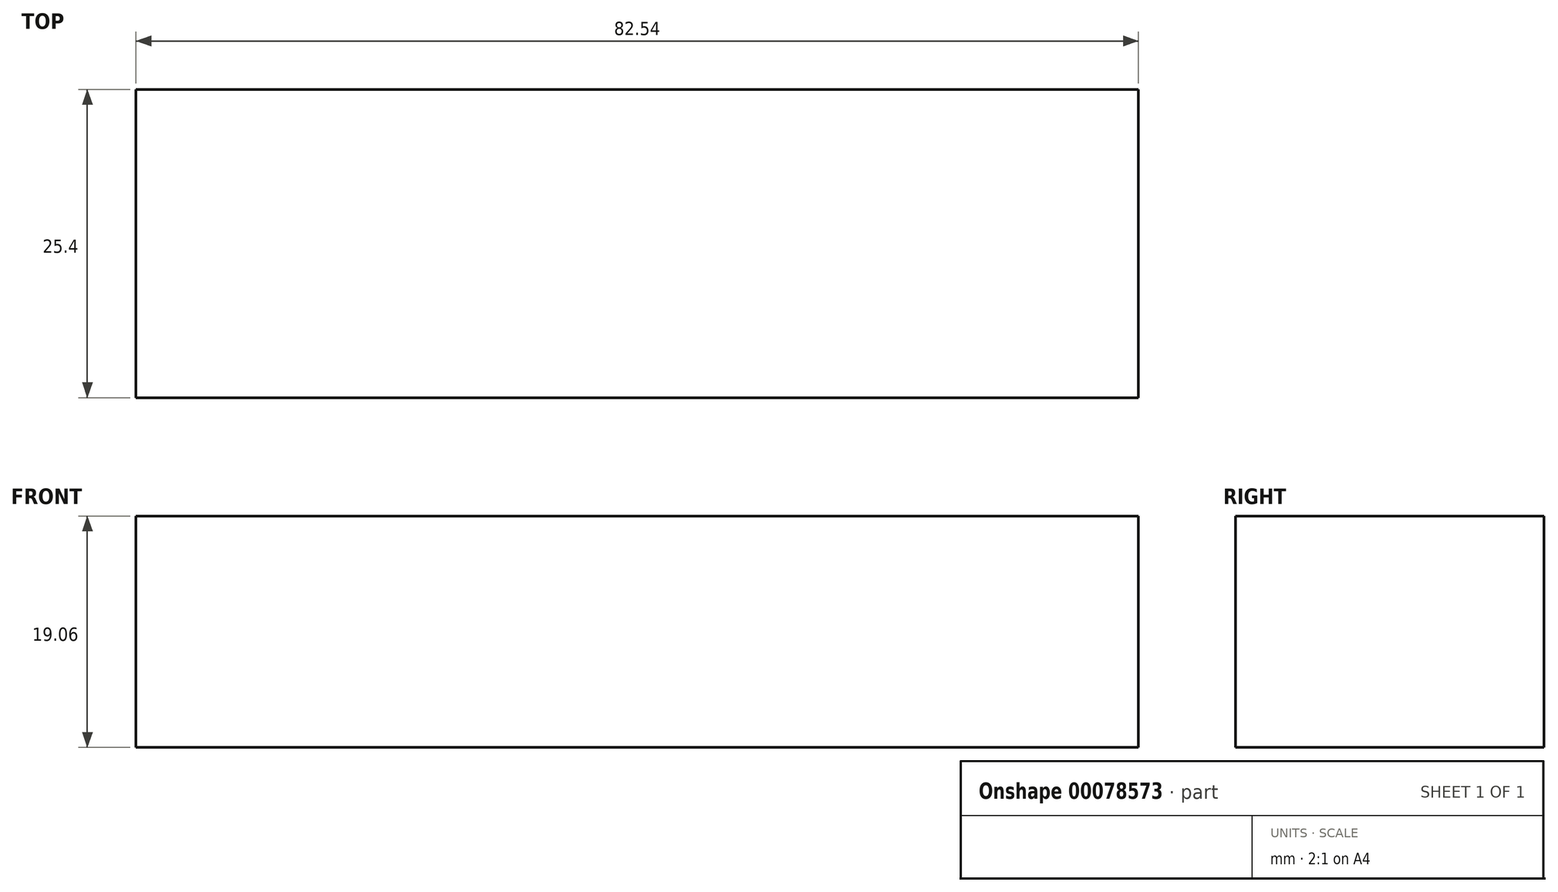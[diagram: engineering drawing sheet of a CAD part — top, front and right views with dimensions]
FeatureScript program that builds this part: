
annotation { "Feature Type Name" : "Feature", "Feature Type Description" : "" }
export const myFeature = defineFeature(function(context is Context, id is Id, definition is map)
    precondition{}
    {
        {
            var Q0;
            Q0=qCreatedBy(makeId("Front.planeOp"),FACE);
            var sketch = newSketch(context, id + "F0", { "sketchPlane" : qUnion([Q0])});
            skLineSegment(sketch, "E0.bottom", {"start": v(41.28, 9.53) * mm, "end": v(-41.28, 9.53) * mm});
            skLineSegment(sketch, "E0.top", {"start": v(41.28, -9.52) * mm, "end": v(-41.27, -9.52) * mm});
            skLineSegment(sketch, "E0.left", {"start": v(41.28, 9.53) * mm, "end": v(41.28, -9.52) * mm});
            skLineSegment(sketch, "E0.right", {"start": v(-41.28, 9.53) * mm, "end": v(-41.27, -9.52) * mm});
            skPoint(sketch, "E0.middle", {"position": v(0, 0) * mm});
            skSolve(sketch);
        }
        {
            var Q0;
            Q0=makeQuery(id+"F0.imprint","IMPRINT",FACE,{"disambiguationData":[TD([[makeQuery(id+"F0.imprint","IMPRINT",EDGE,{"derivedFrom":sQuery(id+"F0.wireOp",EDGE,"E0.bottom")}),1.0]])]});
            extrude(context, id + "F1", {"entities" : qUnion([Q0]), "endBound" : BoundingType.SYMMETRIC, "depth" : 25.4 * mm});
        }
    });
